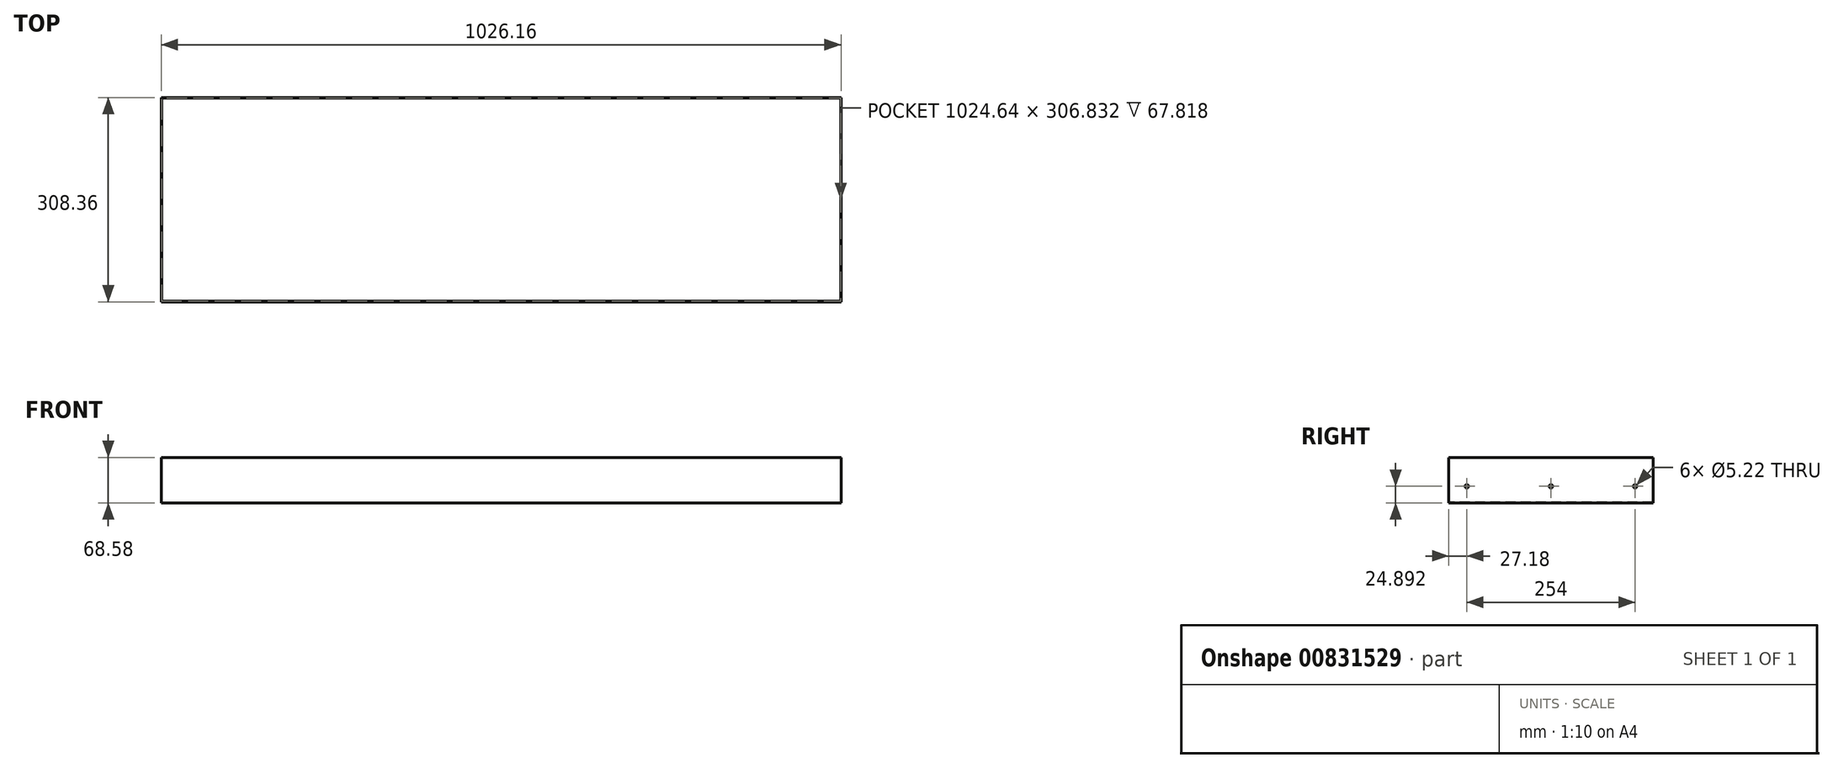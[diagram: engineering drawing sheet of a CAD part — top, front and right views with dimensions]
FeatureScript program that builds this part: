
annotation { "Feature Type Name" : "Feature", "Feature Type Description" : "" }
export const myFeature = defineFeature(function(context is Context, id is Id, definition is map)
    precondition{}
    {
        {
            var Q0;
            Q0=qCreatedBy(makeId("Top.planeOp"),FACE);
            var sketch = newSketch(context, id + "F0", { "sketchPlane" : qUnion([Q0])});
            skLineSegment(sketch, "E0.bottom", {"start": v(-513.08, 154.18) * mm, "end": v(513.08, 154.18) * mm});
            skLineSegment(sketch, "E0.top", {"start": v(-513.08, -154.18) * mm, "end": v(513.08, -154.18) * mm});
            skLineSegment(sketch, "E0.left", {"start": v(-513.08, 154.18) * mm, "end": v(-513.08, -154.18) * mm});
            skLineSegment(sketch, "E0.right", {"start": v(513.08, 154.18) * mm, "end": v(513.08, -154.18) * mm});
            skLineSegment(sketch, "E1", {"start": v(0, 0) * mm, "end": v(-513.08, 0) * mm, "construction": true});
            skLineSegment(sketch, "E2", {"start": v(0, 0) * mm, "end": v(0, 154.18) * mm, "construction": true});
            skSolve(sketch);
        }
        {
            var Q0;
            Q0=makeQuery(id+"F0.imprint","IMPRINT",FACE,{"disambiguationData":[TD([[makeQuery(id+"F0.imprint","IMPRINT",EDGE,{"derivedFrom":sQuery(id+"F0.wireOp",EDGE,"E0.bottom")}),-1.0]])]});
            extrude(context, id + "F1", {"entities" : qUnion([Q0]), "depth" : 68.58 * mm, "offsetDistance" : 25.4 * mm});
        }
        {
            var Q0;
            Q0=makeQuery(id+"F1.opExtrude","CAP_FACE",FACE,{"disambiguationData":[OSD([sQuery(id+"F0.wireOp",EDGE,"E0.bottom"),sQuery(id+"F0.wireOp",EDGE,"E0.top"),sQuery(id+"F0.wireOp",EDGE,"E0.left"),sQuery(id+"F0.wireOp",EDGE,"E0.right")])],"isStart":false});
            shell(context, id + "F2", {"entities" : qUnion([Q0]), "thickness" : 0.76 * mm});
        }
        {
            var Q0;
            Q0=makeQuery(id+"F1.opExtrude","SWEPT_FACE",FACE,{"disambiguationData":[OSD([sQuery(id+"F0.wireOp",EDGE,"E0.left")])]});
            var sketch = newSketch(context, id + "F3", { "sketchPlane" : qUnion([Q0])});
            skPoint(sketch, "E3", {"position": v(-127, 24.9) * mm});
            skPoint(sketch, "E4", {"position": v(0, 24.9) * mm});
            skPoint(sketch, "E5", {"position": v(127, 24.9) * mm});
            skLineSegment(sketch, "E6", {"start": v(0, 68.58) * mm, "end": v(0, 24.9) * mm});
            skLineSegment(sketch, "E7", {"start": v(127, 24.9) * mm, "end": v(0, 24.9) * mm});
            skLineSegment(sketch, "E8", {"start": v(0, 24.9) * mm, "end": v(-127, 24.9) * mm});
            skSolve(sketch);
        }
        {
            var Q0;
            Q0=sQuery(id+"F3.wireOp",VERTEX,"E3");
            var Q1;
            Q1=sQuery(id+"F3.wireOp",VERTEX,"E4");
            var Q2;
            Q2=sQuery(id+"F3.wireOp",VERTEX,"E5");
            var Q3;
            Q3=makeQuery(id+"F1.opExtrude","SWEPT_BODY",BODY,{"disambiguationData":[OSD([sQuery(id+"F0.wireOp",EDGE,"E0.bottom"),sQuery(id+"F0.wireOp",EDGE,"E0.top"),sQuery(id+"F0.wireOp",EDGE,"E0.left"),sQuery(id+"F0.wireOp",EDGE,"E0.right")])]});
            hole(context, id + "F4", {"style" : HoleStyle.SIMPLE, "endStyle" : HoleEndStyle.THROUGH, "standardTappedOrClearance" : lookupTablePath({ "standard" : "ANSI", "size" : "#5 (0.2)", "type" : "Drilled" }), "standardBlindInLast" : lookupTablePath({ "standard" : "ANSI", "size" : "#5 (0.2)", "type" : "Drilled" }), "holeDiameter" : 5.22 * mm, "majorDiameter" : 6.35 * mm, "isTappedThrough" : true, "tappedDepth" : 12.7 * mm, "tapClearance" : 3, "locations" : qUnion([Q0, Q1, Q2]), "scope" : qUnion([Q3])});
        }
    });
